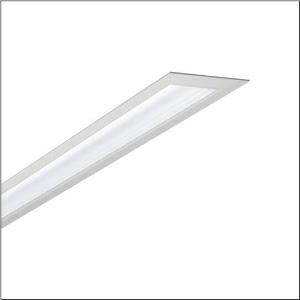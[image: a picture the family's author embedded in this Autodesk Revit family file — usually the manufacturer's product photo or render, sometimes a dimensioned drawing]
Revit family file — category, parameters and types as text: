
# Revit family: silica_r_5mx11dd1w4a_74f3
name_source: partatom
category: Lighting Fixtures
units: mm (PartAtom-declared; Revit-internal decimal feet)

## family parameters
Cut with Voids When Loaded = No
Host = Face
Light Source = No
Part Type = Normal
Room Calculation Point = No
Round Connector Dimension = Use Diameter
Shared = No

## types (1)
- --- (1 x LED, 3140 lm, 22.6 W, 4000K)
    Apparent Load = 23 VA
    CIE Flux Codes = 47 79 96 100 100
    Color Rendering = 80
    Color Temperature = 4000K
    Default Elevation = 1800 mm
    Description = Silica®, office luminaire, of aluminium, opal, light emission: direct distribution, primary light characteristic: symmetric, installation type: recessed, LED, rated luminous flux: 3.010lm, luminous efficacy: 123lm/W, light colour: 840, colour temperature: 4000K, control gear: ECG DALI, with terminal, 3+2-pole, max. 2.5mm², mains connection: 230V, AC, 50/60Hz, rated input power: 24W, luminaire housing, of aluminium, matt pure white (RAL 9010), length: 1.462mm, width: 93mm, height: 60mm, end cap, of diecast zinc, pure white (RAL 9010), protection rating (complete): IP20, insulation class (complete): insulation class I (protective earthing), certification: CE, permissible operating ambient temperature: 0..+35°C, standard: EN 50419, packaging unit: 1 piece
    Height = 0 mm  [stored 0 ft]
    Lamp = 1 x LED
    Lamp Light Flux = 3140 lm
    Lamp Power = 22.6 W
    Lamp count = 1
    Length = 1462 mm
    Luminous efficacy = 139 lm/W
    Manufacturer = Siteco
    ModVariant = No
    Model = 5MX11DD1W4A
    Mounting Place = Ceiling
    Mounting Type = Recessed
    Number of Poles = 1
    OnlyDefault = Yes
    Power Factor = 1
    Product Name = Silica®
    Product group = office luminaire | ceiling recessed
    ProductGroupID = 401
    Protection Class = Protection class I
    Protection Degree = IP 20
    RLX_Detail_Level = 1
    RLX_Emergency_Light_Flux = 0 lm
    RLX_Emergency_Type = 0
    RLX_Emergency_Type_DB = No
    RlxData = <blob elided: 23881 chars, md5=3f6c7161>
    Socket = socket
    Standby Power = 0 W
    System Light Flux = 3140 lm
    System Power = 23 W
    Type Comments = factory setting: luminous flux: 100 % | dim-lin: 254 | 125 mA
    Type Image = l_1004825.jpg
    URL = http://relux.com
    VarID = @adj_135363
    Voltage = 0 V
    Weight = 0.00 kg
    Width = 93 mm

note: [stored X ft] marks values corroborated as IEEE doubles in the binary element streams (Revit-internal decimal feet)

## geometry (parser evidence)
native form markers: Blend x4, Sweep x10
no freeform markers — native parametric forms only
